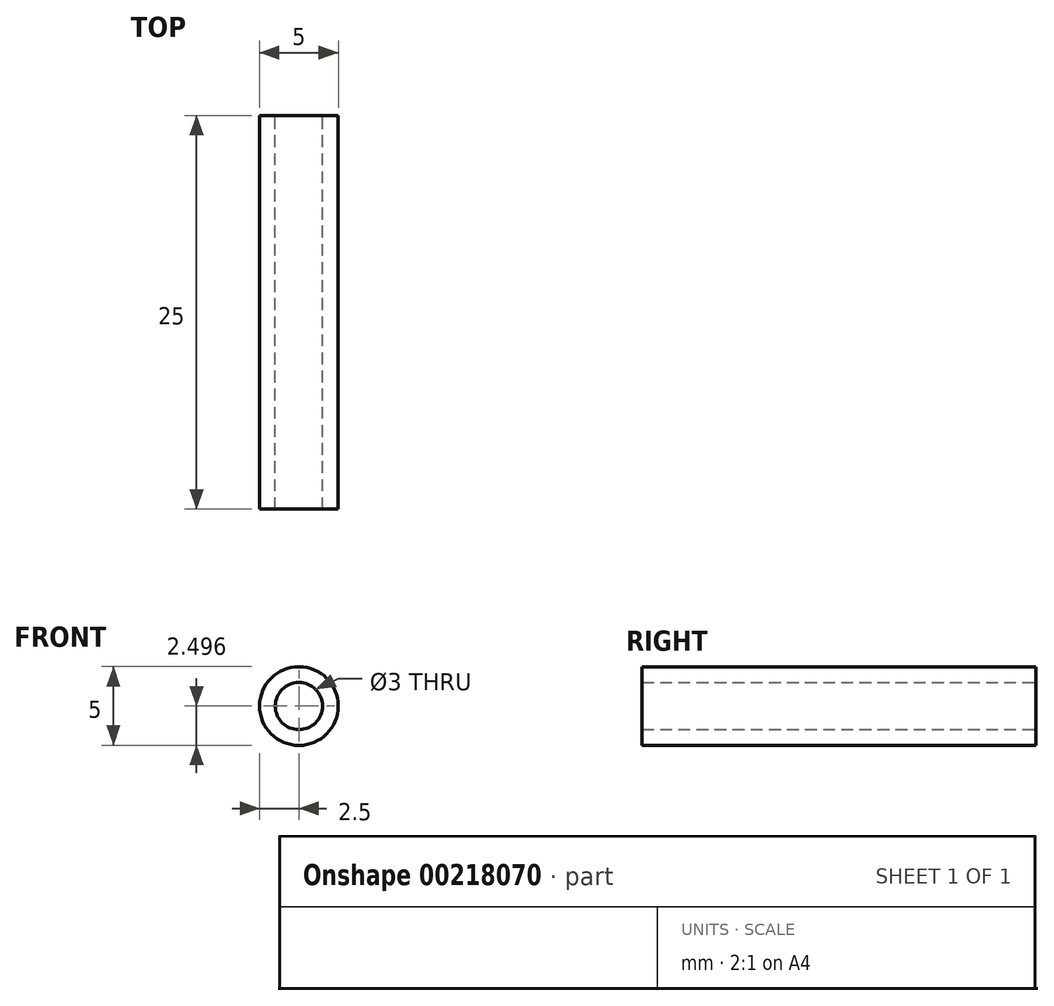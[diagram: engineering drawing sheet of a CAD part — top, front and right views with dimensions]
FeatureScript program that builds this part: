
annotation { "Feature Type Name" : "Feature", "Feature Type Description" : "" }
export const myFeature = defineFeature(function(context is Context, id is Id, definition is map)
    precondition{}
    {
        {
            var Q0;
            Q0=qCreatedBy(makeId("Front.planeOp"),FACE);
            var sketch = newSketch(context, id + "F0", { "sketchPlane" : qUnion([Q0])});
            skArc(sketch, "E0", {"start": v(-41.17, 47.16) * mm, "mid": v(-30.07, -22.2) * mm, "end": v(-18.97, 47.16) * mm});
            skCircle(sketch, "E1", {"center": v(-30.07, 52.72) * mm, "radius": 2 * mm});
            skArc(sketch, "E2", {"start": v(-41.17, 47.16) * mm, "mid": v(-30.07, 46.37) * mm, "end": v(-18.97, 47.16) * mm});
            skCircle(sketch, "E3", {"center": v(-30.07, 13.37) * mm, "radius": 1.5 * mm});
            skLineSegment(sketch, "E4", {"start": v(-30.07, 13.37) * mm, "end": v(-30.07, 60.7) * mm});
            skArc(sketch, "E5", {"start": v(-30.07, 56.28) * mm, "mid": v(-36.97, 53.36) * mm, "end": v(-41.17, 47.16) * mm});
            skPoint(sketch, "E5.startSnap0", {"position": v(-29.45, 56.36) * mm});
            skArc(sketch, "E6.MirrorCS", {"start": v(-30.07, 56.28) * mm, "mid": v(-23.17, 53.36) * mm, "end": v(-18.97, 47.16) * mm});
            skPoint(sketch, "E7.orphan", {"position": v(-31.45, 56.36) * mm});
            skPoint(sketch, "E8.orphan", {"position": v(-28.69, 56.36) * mm});
            skCircle(sketch, "E9", {"center": v(-30.07, 13.37) * mm, "radius": 7.5 * mm});
            skCircle(sketch, "E10", {"center": v(-30.07, 13.37) * mm, "radius": 2.5 * mm});
            skSolve(sketch);
        }
        {
            var Q0;
            {var subQ0=sQuery(id+"F0.wireOp",EDGE,"E0");Q0=makeQuery(id+"F0.imprint","IMPRINT",FACE,{"disambiguationData":[TD([[makeQuery(id+"F0.imprint","IMPRINT",EDGE,{"derivedFrom":subQ0}),1.0]])]});}
            extrude(context, id + "F1", {"entities" : qUnion([Q0]), "depth" : 6 * mm});
        }
        {
            var Q0;
            {var subQ0=sQuery(id+"F0.wireOp",EDGE,"E5");Q0=makeQuery(id+"F0.imprint","IMPRINT",FACE,{"disambiguationData":[TD([[makeQuery(id+"F0.imprint","IMPRINT",EDGE,{"derivedFrom":subQ0}),1.0]])]});}
            var Q1;
            {var subQ0=sQuery(id+"F0.wireOp",EDGE,"E6.MirrorCS");Q1=makeQuery(id+"F0.imprint","IMPRINT",FACE,{"disambiguationData":[TD([[makeQuery(id+"F0.imprint","IMPRINT",EDGE,{"derivedFrom":subQ0}),-1.0]])]});}
            extrude(context, id + "F2", {"entities" : qUnion([Q0, Q1]), "operationType" : NewBodyOperationType.ADD, "depth" : 3 * mm});
        }
        {
            var Q0;
            Q0=makeQuery(id+"F0.imprint","IMPRINT",FACE,{"disambiguationData":[TD([[makeQuery(id+"F0.imprint","IMPRINT",EDGE,{"derivedFrom":sQuery(id+"F0.wireOp",EDGE,"E3")}),-1.0]])]});
            extrude(context, id + "F3", {"entities" : qUnion([Q0]), "depth" : 25 * mm});
        }
        {
            var Q0;
            Q0=makeQuery(id+"F0.imprint","IMPRINT",FACE,{"disambiguationData":[TD([[makeQuery(id+"F0.imprint","IMPRINT",EDGE,{"derivedFrom":sQuery(id+"F0.wireOp",EDGE,"E9")}),1.0]])]});
            extrude(context, id + "F4", {"entities" : qUnion([Q0]), "oppositeDirection" : true, "depth" : 25 * mm});
        }
        {
            var Q0;
            Q0=makeQuery(id+"F1.opExtrude","SWEPT_BODY",BODY,{"disambiguationData":[OSD([sQuery(id+"F0.wireOp",EDGE,"E0"),sQuery(id+"F0.wireOp",EDGE,"E2"),sQuery(id+"F0.wireOp",EDGE,"E9")])]});
            deleteBodies(context, id + "F5", {"entities" : qUnion([Q0])});
        }
        {
            var Q0;
            Q0=makeQuery(id+"F4.opExtrude","SWEPT_BODY",BODY,{"disambiguationData":[OSD([sQuery(id+"F0.wireOp",EDGE,"E9"),sQuery(id+"F0.wireOp",EDGE,"E10")])]});
            deleteBodies(context, id + "F6", {"entities" : qUnion([Q0])});
        }
    });
